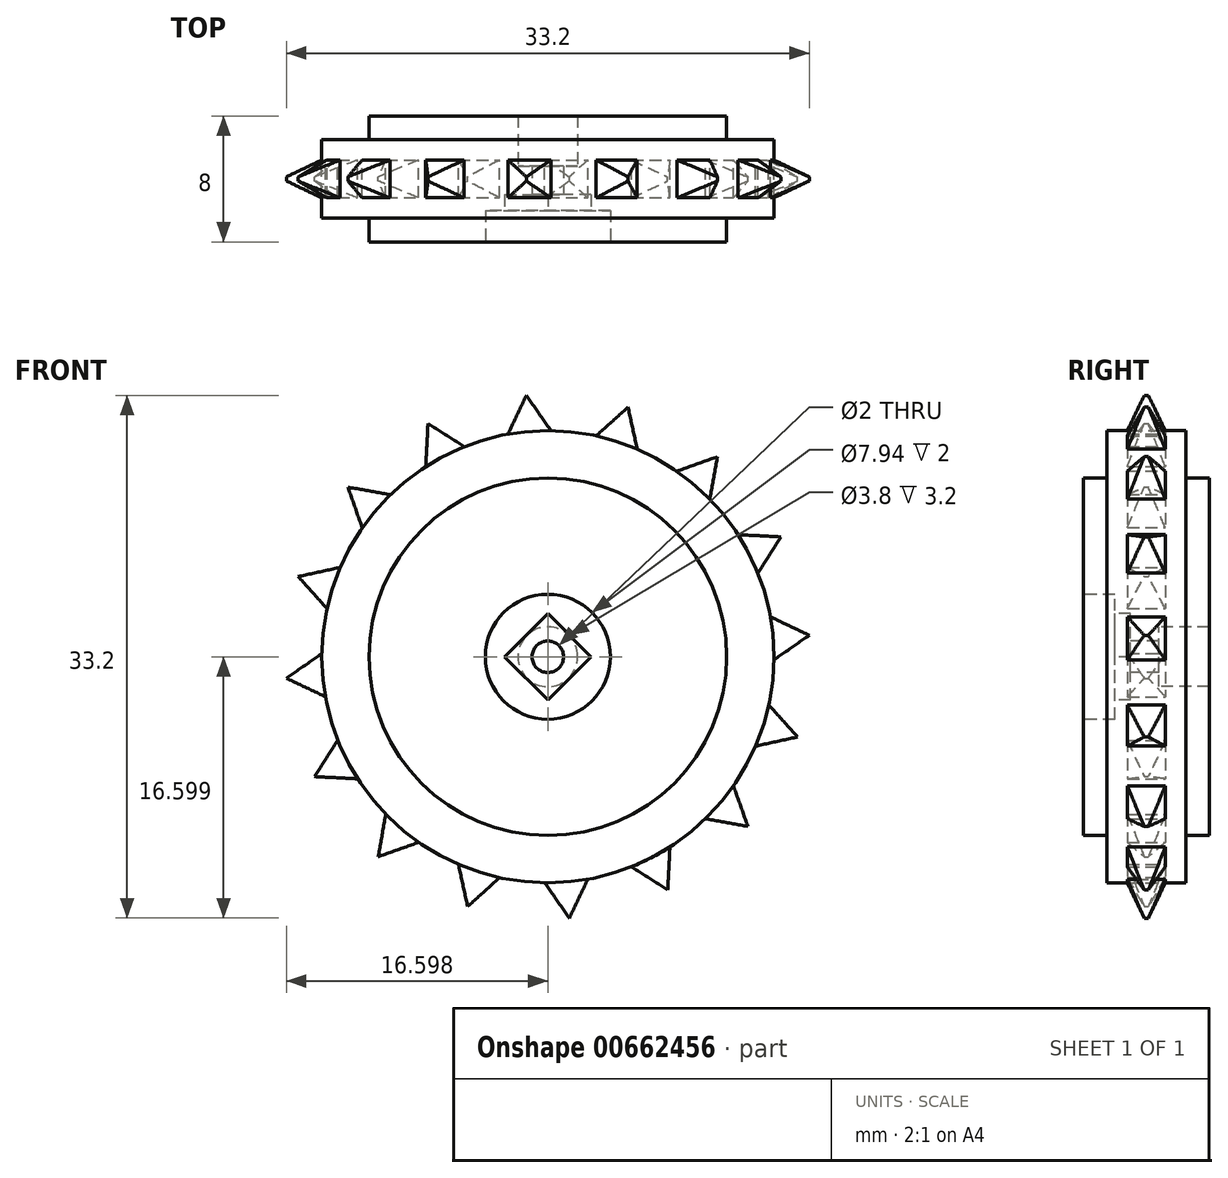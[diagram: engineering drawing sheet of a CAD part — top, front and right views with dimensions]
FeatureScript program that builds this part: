
annotation { "Feature Type Name" : "Feature", "Feature Type Description" : "" }
export const myFeature = defineFeature(function(context is Context, id is Id, definition is map)
    precondition{}
    {
        {
            var Q0;
            Q0=qCreatedBy(makeId("Front.planeOp"),FACE);
            var sketch = newSketch(context, id + "F0", { "sketchPlane" : qUnion([Q0])});
            skPoint(sketch, "E0", {"position": v(-41.55, 40.69) * mm});
            skCircle(sketch, "E1.cCircle", {"center": v(-41.55, 40.69) * mm, "radius": 16.34 * mm, "construction": true});
            skLineSegment(sketch, "E1.0", {"start": v(-36.46, 56.55) * mm, "end": v(-30.78, 53.4) * mm});
            skLineSegment(sketch, "E1.1", {"start": v(-30.78, 53.4) * mm, "end": v(-26.73, 48.3) * mm});
            skLineSegment(sketch, "E1.2", {"start": v(-26.73, 48.3) * mm, "end": v(-24.95, 42.05) * mm});
            skLineSegment(sketch, "E1.3", {"start": v(-24.95, 42.05) * mm, "end": v(-25.7, 35.6) * mm});
            skLineSegment(sketch, "E1.4", {"start": v(-25.7, 35.6) * mm, "end": v(-28.85, 29.91) * mm});
            skLineSegment(sketch, "E1.5", {"start": v(-28.85, 29.91) * mm, "end": v(-33.94, 25.87) * mm});
            skLineSegment(sketch, "E1.6", {"start": v(-33.94, 25.87) * mm, "end": v(-40.19, 24.09) * mm});
            skLineSegment(sketch, "E1.7", {"start": v(-40.19, 24.09) * mm, "end": v(-46.65, 24.83) * mm});
            skLineSegment(sketch, "E1.8", {"start": v(-46.65, 24.83) * mm, "end": v(-52.33, 27.98) * mm});
            skLineSegment(sketch, "E1.9", {"start": v(-52.33, 27.98) * mm, "end": v(-56.37, 33.08) * mm});
            skLineSegment(sketch, "E1.10", {"start": v(-56.37, 33.08) * mm, "end": v(-58.15, 39.33) * mm});
            skLineSegment(sketch, "E1.11", {"start": v(-58.15, 39.33) * mm, "end": v(-57.41, 45.78) * mm});
            skLineSegment(sketch, "E1.12", {"start": v(-57.41, 45.78) * mm, "end": v(-54.26, 51.46) * mm});
            skLineSegment(sketch, "E1.13", {"start": v(-54.26, 51.46) * mm, "end": v(-49.17, 55.5) * mm});
            skLineSegment(sketch, "E1.14", {"start": v(-49.17, 55.5) * mm, "end": v(-42.92, 57.3) * mm});
            skLineSegment(sketch, "E1.15", {"start": v(-42.92, 57.3) * mm, "end": v(-36.46, 56.55) * mm});
            skPoint(sketch, "E1.0.midPoint", {"position": v(-33.62, 54.97) * mm});
            skLineSegment(sketch, "E2", {"start": v(-41.55, 40.69) * mm, "end": v(-42.92, 57.3) * mm, "construction": true});
            skPoint(sketch, "E3", {"position": v(-42.69, 54.5) * mm});
            skPoint(sketch, "E4", {"position": v(-42.73, 55) * mm});
            skLineSegment(sketch, "E5", {"start": v(-42.92, 57.3) * mm, "end": v(-44.24, 54.5) * mm});
            skLineSegment(sketch, "E6.MirrorCS", {"start": v(-42.92, 57.3) * mm, "end": v(-41.15, 54.76) * mm});
            skPoint(sketch, "E7", {"position": v(-42.48, 52) * mm});
            skLineSegment(sketch, "E8.1.0", {"start": v(-49.17, 55.5) * mm, "end": v(-49.32, 52.42) * mm});
            skLineSegment(sketch, "E8.1.1", {"start": v(-49.17, 55.5) * mm, "end": v(-46.56, 53.84) * mm});
            skLineSegment(sketch, "E8.2.0", {"start": v(-54.26, 51.46) * mm, "end": v(-53.22, 48.55) * mm});
            skLineSegment(sketch, "E8.2.1", {"start": v(-54.26, 51.46) * mm, "end": v(-51.21, 50.92) * mm});
            skLineSegment(sketch, "E8.3.0", {"start": v(-57.41, 45.78) * mm, "end": v(-55.34, 43.49) * mm});
            skLineSegment(sketch, "E8.3.1", {"start": v(-57.41, 45.78) * mm, "end": v(-54.4, 46.44) * mm});
            skLineSegment(sketch, "E8.4.0", {"start": v(-58.15, 39.33) * mm, "end": v(-55.36, 38) * mm});
            skLineSegment(sketch, "E8.4.1", {"start": v(-58.15, 39.33) * mm, "end": v(-55.62, 41.1) * mm});
            skLineSegment(sketch, "E8.5.0", {"start": v(-56.37, 33.08) * mm, "end": v(-53.28, 32.92) * mm});
            skLineSegment(sketch, "E8.5.1", {"start": v(-56.37, 33.08) * mm, "end": v(-54.7, 35.68) * mm});
            skLineSegment(sketch, "E8.6.0", {"start": v(-52.33, 27.98) * mm, "end": v(-49.42, 29.02) * mm});
            skLineSegment(sketch, "E8.6.1", {"start": v(-52.33, 27.98) * mm, "end": v(-51.78, 31.03) * mm});
            skLineSegment(sketch, "E8.7.0", {"start": v(-46.65, 24.83) * mm, "end": v(-44.35, 26.9) * mm});
            skLineSegment(sketch, "E8.7.1", {"start": v(-46.65, 24.83) * mm, "end": v(-47.3, 27.85) * mm});
            skLineSegment(sketch, "E8.8.0", {"start": v(-40.19, 24.09) * mm, "end": v(-38.86, 26.88) * mm});
            skLineSegment(sketch, "E8.8.1", {"start": v(-40.19, 24.09) * mm, "end": v(-41.95, 26.62) * mm});
            skLineSegment(sketch, "E8.9.0", {"start": v(-33.94, 25.87) * mm, "end": v(-33.78, 28.96) * mm});
            skLineSegment(sketch, "E8.9.1", {"start": v(-33.94, 25.87) * mm, "end": v(-36.54, 27.54) * mm});
            skLineSegment(sketch, "E8.10.0", {"start": v(-28.85, 29.91) * mm, "end": v(-29.88, 32.83) * mm});
            skLineSegment(sketch, "E8.10.1", {"start": v(-28.85, 29.91) * mm, "end": v(-31.89, 30.46) * mm});
            skLineSegment(sketch, "E8.11.0", {"start": v(-25.7, 35.6) * mm, "end": v(-27.76, 37.89) * mm});
            skLineSegment(sketch, "E8.11.1", {"start": v(-25.7, 35.6) * mm, "end": v(-28.7, 34.94) * mm});
            skLineSegment(sketch, "E8.12.0", {"start": v(-24.95, 42.05) * mm, "end": v(-27.74, 43.38) * mm});
            skLineSegment(sketch, "E8.12.1", {"start": v(-24.95, 42.05) * mm, "end": v(-27.49, 40.29) * mm});
            skLineSegment(sketch, "E8.13.0", {"start": v(-26.73, 48.3) * mm, "end": v(-29.82, 48.46) * mm});
            skLineSegment(sketch, "E8.13.1", {"start": v(-26.73, 48.3) * mm, "end": v(-28.4, 45.7) * mm});
            skLineSegment(sketch, "E8.14.0", {"start": v(-30.78, 53.4) * mm, "end": v(-33.69, 52.36) * mm});
            skLineSegment(sketch, "E8.14.1", {"start": v(-30.78, 53.4) * mm, "end": v(-31.32, 50.35) * mm});
            skLineSegment(sketch, "E8.15.0", {"start": v(-36.46, 56.55) * mm, "end": v(-38.75, 54.48) * mm});
            skLineSegment(sketch, "E8.15.1", {"start": v(-36.46, 56.55) * mm, "end": v(-35.8, 53.53) * mm});
            skCircle(sketch, "E9", {"center": v(-41.55, 40.69) * mm, "radius": 11.36 * mm});
            skCircle(sketch, "E10", {"center": v(-41.55, 40.69) * mm, "radius": 14.36 * mm});
            skSolve(sketch);
        }
        {
            var Q0;
            {var subQ1=sQuery(id+"F0.wireOp",EDGE,"E8.12.0");var subQ3=sQuery(id+"F0.wireOp",EDGE,"E10");var subQ4=makeQuery(id+"F0.imprint","INTERSECT",VERTEX,{"derivedFrom":[subQ1,subQ3]});Q0=makeQuery(id+"F0.imprint","IMPRINT",FACE,{"disambiguationData":[TD([[makeQuery(id+"F0.imprint","IMPRINT",EDGE,{"disambiguationData":[TD([[subQ4,1.0]])],"derivedFrom":subQ3}),-1.0]])]});}
            var Q1;
            {var subQ1=sQuery(id+"F0.wireOp",EDGE,"E8.11.0");var subQ3=sQuery(id+"F0.wireOp",EDGE,"E10");var subQ4=makeQuery(id+"F0.imprint","INTERSECT",VERTEX,{"derivedFrom":[subQ1,subQ3]});Q1=makeQuery(id+"F0.imprint","IMPRINT",FACE,{"disambiguationData":[TD([[makeQuery(id+"F0.imprint","IMPRINT",EDGE,{"disambiguationData":[TD([[subQ4,1.0]])],"derivedFrom":subQ3}),-1.0]])]});}
            var Q2;
            {var subQ1=sQuery(id+"F0.wireOp",EDGE,"E8.10.0");var subQ3=sQuery(id+"F0.wireOp",EDGE,"E10");var subQ4=makeQuery(id+"F0.imprint","INTERSECT",VERTEX,{"derivedFrom":[subQ1,subQ3]});Q2=makeQuery(id+"F0.imprint","IMPRINT",FACE,{"disambiguationData":[TD([[makeQuery(id+"F0.imprint","IMPRINT",EDGE,{"disambiguationData":[TD([[subQ4,1.0]])],"derivedFrom":subQ3}),-1.0]])]});}
            var Q3;
            {var subQ1=sQuery(id+"F0.wireOp",EDGE,"E8.9.0");var subQ3=sQuery(id+"F0.wireOp",EDGE,"E10");var subQ4=makeQuery(id+"F0.imprint","INTERSECT",VERTEX,{"derivedFrom":[subQ1,subQ3]});Q3=makeQuery(id+"F0.imprint","IMPRINT",FACE,{"disambiguationData":[TD([[makeQuery(id+"F0.imprint","IMPRINT",EDGE,{"disambiguationData":[TD([[subQ4,1.0]])],"derivedFrom":subQ3}),-1.0]])]});}
            var Q4;
            {var subQ1=sQuery(id+"F0.wireOp",EDGE,"E8.8.0");var subQ3=sQuery(id+"F0.wireOp",EDGE,"E10");var subQ4=makeQuery(id+"F0.imprint","INTERSECT",VERTEX,{"derivedFrom":[subQ1,subQ3]});Q4=makeQuery(id+"F0.imprint","IMPRINT",FACE,{"disambiguationData":[TD([[makeQuery(id+"F0.imprint","IMPRINT",EDGE,{"disambiguationData":[TD([[subQ4,1.0]])],"derivedFrom":subQ3}),-1.0]])]});}
            var Q5;
            {var subQ1=sQuery(id+"F0.wireOp",EDGE,"E8.7.0");var subQ3=sQuery(id+"F0.wireOp",EDGE,"E10");var subQ4=makeQuery(id+"F0.imprint","INTERSECT",VERTEX,{"derivedFrom":[subQ1,subQ3]});Q5=makeQuery(id+"F0.imprint","IMPRINT",FACE,{"disambiguationData":[TD([[makeQuery(id+"F0.imprint","IMPRINT",EDGE,{"disambiguationData":[TD([[subQ4,1.0]])],"derivedFrom":subQ3}),-1.0]])]});}
            var Q6;
            {var subQ1=sQuery(id+"F0.wireOp",EDGE,"E8.6.0");var subQ3=sQuery(id+"F0.wireOp",EDGE,"E10");var subQ4=makeQuery(id+"F0.imprint","INTERSECT",VERTEX,{"derivedFrom":[subQ1,subQ3]});Q6=makeQuery(id+"F0.imprint","IMPRINT",FACE,{"disambiguationData":[TD([[makeQuery(id+"F0.imprint","IMPRINT",EDGE,{"disambiguationData":[TD([[subQ4,1.0]])],"derivedFrom":subQ3}),-1.0]])]});}
            var Q7;
            {var subQ1=sQuery(id+"F0.wireOp",EDGE,"E8.5.0");var subQ3=sQuery(id+"F0.wireOp",EDGE,"E10");var subQ4=makeQuery(id+"F0.imprint","INTERSECT",VERTEX,{"derivedFrom":[subQ1,subQ3]});Q7=makeQuery(id+"F0.imprint","IMPRINT",FACE,{"disambiguationData":[TD([[makeQuery(id+"F0.imprint","IMPRINT",EDGE,{"disambiguationData":[TD([[subQ4,1.0]])],"derivedFrom":subQ3}),-1.0]])]});}
            var Q8;
            {var subQ1=sQuery(id+"F0.wireOp",EDGE,"E8.4.0");var subQ3=sQuery(id+"F0.wireOp",EDGE,"E10");var subQ4=makeQuery(id+"F0.imprint","INTERSECT",VERTEX,{"derivedFrom":[subQ1,subQ3]});Q8=makeQuery(id+"F0.imprint","IMPRINT",FACE,{"disambiguationData":[TD([[makeQuery(id+"F0.imprint","IMPRINT",EDGE,{"disambiguationData":[TD([[subQ4,1.0]])],"derivedFrom":subQ3}),-1.0]])]});}
            var Q9;
            {var subQ1=sQuery(id+"F0.wireOp",EDGE,"E8.3.0");var subQ3=sQuery(id+"F0.wireOp",EDGE,"E10");var subQ4=makeQuery(id+"F0.imprint","INTERSECT",VERTEX,{"derivedFrom":[subQ1,subQ3]});Q9=makeQuery(id+"F0.imprint","IMPRINT",FACE,{"disambiguationData":[TD([[makeQuery(id+"F0.imprint","IMPRINT",EDGE,{"disambiguationData":[TD([[subQ4,1.0]])],"derivedFrom":subQ3}),-1.0]])]});}
            var Q10;
            {var subQ1=sQuery(id+"F0.wireOp",EDGE,"E8.2.0");var subQ3=sQuery(id+"F0.wireOp",EDGE,"E10");var subQ4=makeQuery(id+"F0.imprint","INTERSECT",VERTEX,{"derivedFrom":[subQ1,subQ3]});Q10=makeQuery(id+"F0.imprint","IMPRINT",FACE,{"disambiguationData":[TD([[makeQuery(id+"F0.imprint","IMPRINT",EDGE,{"disambiguationData":[TD([[subQ4,1.0]])],"derivedFrom":subQ3}),-1.0]])]});}
            var Q11;
            {var subQ1=sQuery(id+"F0.wireOp",EDGE,"E8.1.0");var subQ3=sQuery(id+"F0.wireOp",EDGE,"E10");var subQ4=makeQuery(id+"F0.imprint","INTERSECT",VERTEX,{"derivedFrom":[subQ1,subQ3]});Q11=makeQuery(id+"F0.imprint","IMPRINT",FACE,{"disambiguationData":[TD([[makeQuery(id+"F0.imprint","IMPRINT",EDGE,{"disambiguationData":[TD([[subQ4,1.0]])],"derivedFrom":subQ3}),-1.0]])]});}
            var Q12;
            {var subQ1=sQuery(id+"F0.wireOp",EDGE,"E5");var subQ3=sQuery(id+"F0.wireOp",EDGE,"E10");var subQ4=makeQuery(id+"F0.imprint","INTERSECT",VERTEX,{"derivedFrom":[subQ1,subQ3]});Q12=makeQuery(id+"F0.imprint","IMPRINT",FACE,{"disambiguationData":[TD([[makeQuery(id+"F0.imprint","IMPRINT",EDGE,{"disambiguationData":[TD([[subQ4,1.0]])],"derivedFrom":subQ3}),-1.0]])]});}
            var Q13;
            {var subQ1=sQuery(id+"F0.wireOp",EDGE,"E8.15.0");var subQ3=sQuery(id+"F0.wireOp",EDGE,"E10");var subQ4=makeQuery(id+"F0.imprint","INTERSECT",VERTEX,{"derivedFrom":[subQ1,subQ3]});Q13=makeQuery(id+"F0.imprint","IMPRINT",FACE,{"disambiguationData":[TD([[makeQuery(id+"F0.imprint","IMPRINT",EDGE,{"disambiguationData":[TD([[subQ4,1.0]])],"derivedFrom":subQ3}),-1.0]])]});}
            var Q14;
            {var subQ1=sQuery(id+"F0.wireOp",EDGE,"E8.14.0");var subQ3=sQuery(id+"F0.wireOp",EDGE,"E10");var subQ4=makeQuery(id+"F0.imprint","INTERSECT",VERTEX,{"derivedFrom":[subQ1,subQ3]});Q14=makeQuery(id+"F0.imprint","IMPRINT",FACE,{"disambiguationData":[TD([[makeQuery(id+"F0.imprint","IMPRINT",EDGE,{"disambiguationData":[TD([[subQ4,1.0]])],"derivedFrom":subQ3}),-1.0]])]});}
            var Q15;
            {var subQ1=sQuery(id+"F0.wireOp",EDGE,"E8.13.0");var subQ3=sQuery(id+"F0.wireOp",EDGE,"E10");var subQ4=makeQuery(id+"F0.imprint","INTERSECT",VERTEX,{"derivedFrom":[subQ1,subQ3]});Q15=makeQuery(id+"F0.imprint","IMPRINT",FACE,{"disambiguationData":[TD([[makeQuery(id+"F0.imprint","IMPRINT",EDGE,{"disambiguationData":[TD([[subQ4,1.0]])],"derivedFrom":subQ3}),-1.0]])]});}
            var Q16;
            Q16=makeQuery(id+"F0.imprint","IMPRINT",FACE,{"disambiguationData":[TD([[makeQuery(id+"F0.imprint","IMPRINT",EDGE,{"derivedFrom":sQuery(id+"F0.wireOp",EDGE,"E9")}),-1.0]])]});
            var Q17;
            Q17=makeQuery(id+"F0.imprint","IMPRINT",FACE,{"disambiguationData":[TD([[makeQuery(id+"F0.imprint","IMPRINT",EDGE,{"derivedFrom":sQuery(id+"F0.wireOp",EDGE,"E9")}),1.0]])]});
            extrude(context, id + "F1", {"entities" : qUnion([Q0, Q1, Q2, Q3, Q4, Q5, Q6, Q7, Q8, Q9, Q10, Q11, Q12, Q13, Q14, Q15, Q16, Q17]), "endBound" : BoundingType.SYMMETRIC, "depth" : 2.4 * mm, "offsetDistance" : 25 * mm});
        }
        {
            var Q0;
            Q0=makeQuery(id+"F0.imprint","IMPRINT",FACE,{"disambiguationData":[TD([[makeQuery(id+"F0.imprint","IMPRINT",EDGE,{"derivedFrom":sQuery(id+"F0.wireOp",EDGE,"E9")}),-1.0]])]});
            var Q1;
            Q1=makeQuery(id+"F0.imprint","IMPRINT",FACE,{"disambiguationData":[TD([[makeQuery(id+"F0.imprint","IMPRINT",EDGE,{"derivedFrom":sQuery(id+"F0.wireOp",EDGE,"E9")}),1.0]])]});
            extrude(context, id + "F2", {"entities" : qUnion([Q0, Q1]), "operationType" : NewBodyOperationType.ADD, "endBound" : BoundingType.SYMMETRIC, "depth" : 5 * mm, "offsetDistance" : 25 * mm});
        }
        {
            var Q0;
            Q0=makeQuery(id+"F0.imprint","IMPRINT",FACE,{"disambiguationData":[TD([[makeQuery(id+"F0.imprint","IMPRINT",EDGE,{"derivedFrom":sQuery(id+"F0.wireOp",EDGE,"E9")}),1.0]])]});
            extrude(context, id + "F3", {"entities" : qUnion([Q0]), "operationType" : NewBodyOperationType.ADD, "endBound" : BoundingType.SYMMETRIC, "depth" : 8 * mm, "offsetDistance" : 25 * mm});
        }
        {
            var Q0;
            Q0=makeQuery(id+"F3.opExtrude","CAP_FACE",FACE,{"disambiguationData":[OSD([sQuery(id+"F0.wireOp",EDGE,"E9")])],"isStart":false});
            var sketch = newSketch(context, id + "F4", { "sketchPlane" : qUnion([Q0])});
            skCircle(sketch, "E11.0", {"center": v(-41.55, 40.69) * mm, "radius": 11.36 * mm});
            skCircle(sketch, "E12.cCircle", {"center": v(-41.55, 40.69) * mm, "radius": 2.75 * mm, "construction": true});
            skLineSegment(sketch, "E12.0", {"start": v(-44.3, 40.69) * mm, "end": v(-41.55, 43.44) * mm});
            skLineSegment(sketch, "E12.1", {"start": v(-41.55, 43.44) * mm, "end": v(-38.8, 40.69) * mm});
            skLineSegment(sketch, "E12.2", {"start": v(-38.8, 40.69) * mm, "end": v(-41.55, 37.94) * mm});
            skLineSegment(sketch, "E12.3", {"start": v(-41.55, 37.94) * mm, "end": v(-44.3, 40.69) * mm});
            skCircle(sketch, "E13", {"center": v(-41.55, 40.69) * mm, "radius": 1 * mm});
            skCircle(sketch, "E14", {"center": v(-41.55, 40.69) * mm, "radius": 3.97 * mm});
            skPoint(sketch, "E15.0", {"position": v(-54.26, 51.46) * mm});
            skLineSegment(sketch, "E16", {"start": v(-41.55, 40.69) * mm, "end": v(-54.26, 51.46) * mm});
            skSolve(sketch);
        }
        {
            var Q0;
            Q0=makeQuery(id+"F4.imprint","IMPRINT",FACE,{"disambiguationData":[TD([[makeQuery(id+"F4.imprint","IMPRINT",EDGE,{"derivedFrom":sQuery(id+"F4.wireOp",EDGE,"E13")}),1.0]])]});
            extrude(context, id + "F5", {"entities" : qUnion([Q0]), "operationType" : NewBodyOperationType.REMOVE, "oppositeDirection" : true, "depth" : 25 * mm, "offsetDistance" : 25 * mm});
        }
        {
            var Q0;
            Q0=makeQuery(id+"F4.imprint","IMPRINT",FACE,{"disambiguationData":[TD([[makeQuery(id+"F4.imprint","IMPRINT",EDGE,{"derivedFrom":sQuery(id+"F4.wireOp",EDGE,"E12.0")}),-1.0]])]});
            extrude(context, id + "F6", {"entities" : qUnion([Q0]), "operationType" : NewBodyOperationType.REMOVE, "oppositeDirection" : true, "depth" : 3 * mm, "offsetDistance" : 25 * mm});
        }
        {
            var Q0;
            Q0=makeQuery(id+"F4.imprint","IMPRINT",FACE,{"disambiguationData":[TD([[makeQuery(id+"F4.imprint","IMPRINT",EDGE,{"derivedFrom":sQuery(id+"F4.wireOp",EDGE,"E12.0")}),1.0]])]});
            extrude(context, id + "F7", {"entities" : qUnion([Q0]), "operationType" : NewBodyOperationType.REMOVE, "oppositeDirection" : true, "depth" : 2 * mm, "offsetDistance" : 25 * mm});
        }
        {
            var Q0;
            Q0=sQuery(id+"F4.wireOp",EDGE,"E16");
            extrude(context, id + "F8", {"bodyType" : ToolBodyType.SURFACE, "surfaceEntities" : qUnion([Q0]), "oppositeDirection" : true, "depth" : 8 * mm, "offsetDistance" : 25 * mm});
        }
        {
            var Q0;
            Q0=makeQuery(id+"F6.boolean.opBoolean","COPY",FACE,{"derivedFrom":makeQuery(id+"F6.opExtrude","CAP_FACE",FACE,{"disambiguationData":[OSD([sQuery(id+"F4.wireOp",EDGE,"E12.0"),sQuery(id+"F4.wireOp",EDGE,"E12.1"),sQuery(id+"F4.wireOp",EDGE,"E12.2"),sQuery(id+"F4.wireOp",EDGE,"E12.3"),sQuery(id+"F4.wireOp",EDGE,"E13")])],"isStart":false})});
            var sketch = newSketch(context, id + "F9", { "sketchPlane" : qUnion([Q0])});
            skCircle(sketch, "E17.0", {"center": v(-41.55, 40.69) * mm, "radius": 1 * mm});
            skCircle(sketch, "E18", {"center": v(-41.55, 40.69) * mm, "radius": 1.9 * mm});
            skSolve(sketch);
        }
        {
            var Q0;
            Q0=makeQuery(id+"F9.imprint","IMPRINT",FACE,{"disambiguationData":[TD([[makeQuery(id+"F9.imprint","IMPRINT",EDGE,{"derivedFrom":sQuery(id+"F9.wireOp",EDGE,"E17.0")}),-1.0]])]});
            extrude(context, id + "F10", {"entities" : qUnion([Q0]), "operationType" : NewBodyOperationType.REMOVE, "oppositeDirection" : true, "depth" : 7.6 * mm, "offsetDistance" : 25 * mm, "hasSecondDirection" : true, "secondDirectionOppositeDirection" : true, "secondDirectionDepth" : 1.8 * mm});
        }
        {
            var Q0;
            Q0=makeQuery(id+"F8.opExtrude","SWEPT_FACE",FACE,{"disambiguationData":[OSD([sQuery(id+"F4.wireOp",EDGE,"E16")])]});
            var sketch = newSketch(context, id + "F11", { "sketchPlane" : qUnion([Q0])});
            skPoint(sketch, "E19.0", {"position": v(-74.67, 1.2) * mm});
            skPoint(sketch, "E19.1", {"position": v(-74.67, -1.2) * mm});
            skPoint(sketch, "E19.2", {"position": v(-72.37, 1.2) * mm});
            skPoint(sketch, "E19.3", {"position": v(-72.37, -1.2) * mm});
            skPoint(sketch, "E20", {"position": v(-74.67, 0) * mm});
            skLineSegment(sketch, "E21", {"start": v(-72.37, 1.2) * mm, "end": v(-74.67, 0.12) * mm});
            skLineSegment(sketch, "E22", {"start": v(-74.67, 0.12) * mm, "end": v(-74.67, 1.2) * mm});
            skLineSegment(sketch, "E23", {"start": v(-72.37, 1.2) * mm, "end": v(-74.67, 1.2) * mm});
            skLineSegment(sketch, "E24", {"start": v(-75.51, 0) * mm, "end": v(-71.94, 0) * mm, "construction": true});
            skLineSegment(sketch, "E25.MirrorCS", {"start": v(-72.37, -1.2) * mm, "end": v(-74.67, -0.12) * mm});
            skLineSegment(sketch, "E26.MirrorCS", {"start": v(-74.67, -0.12) * mm, "end": v(-74.67, -1.2) * mm});
            skLineSegment(sketch, "E27.MirrorCS", {"start": v(-72.37, -1.2) * mm, "end": v(-74.67, -1.2) * mm});
            skSolve(sketch);
        }
        {
            var Q0;
            Q0=makeQuery(id+"F11.imprint","IMPRINT",FACE,{"disambiguationData":[TD([[makeQuery(id+"F11.imprint","IMPRINT",EDGE,{"derivedFrom":sQuery(id+"F11.wireOp",EDGE,"E21")}),-1.0]])]});
            var Q1;
            Q1=makeQuery(id+"F11.imprint","IMPRINT",FACE,{"disambiguationData":[TD([[makeQuery(id+"F11.imprint","IMPRINT",EDGE,{"derivedFrom":sQuery(id+"F11.wireOp",EDGE,"E25.MirrorCS")}),1.0]])]});
            var Q2;
            Q2=makeQuery(id+"F8.opExtrude","SWEPT_EDGE",EDGE,{"disambiguationData":[OSD([sQuery(id+"F4.wireOp",VERTEX,"E16.start")])]});
            revolve(context, id + "F12", {"operationType" : NewBodyOperationType.REMOVE, "surfaceOperationType" : NewSurfaceOperationType.NEW, "entities" : qUnion([Q0, Q1]), "axis" : qUnion([Q2]), "revolveType" : RevolveType.FULL, "oppositeDirection" : true});
        }
    });
